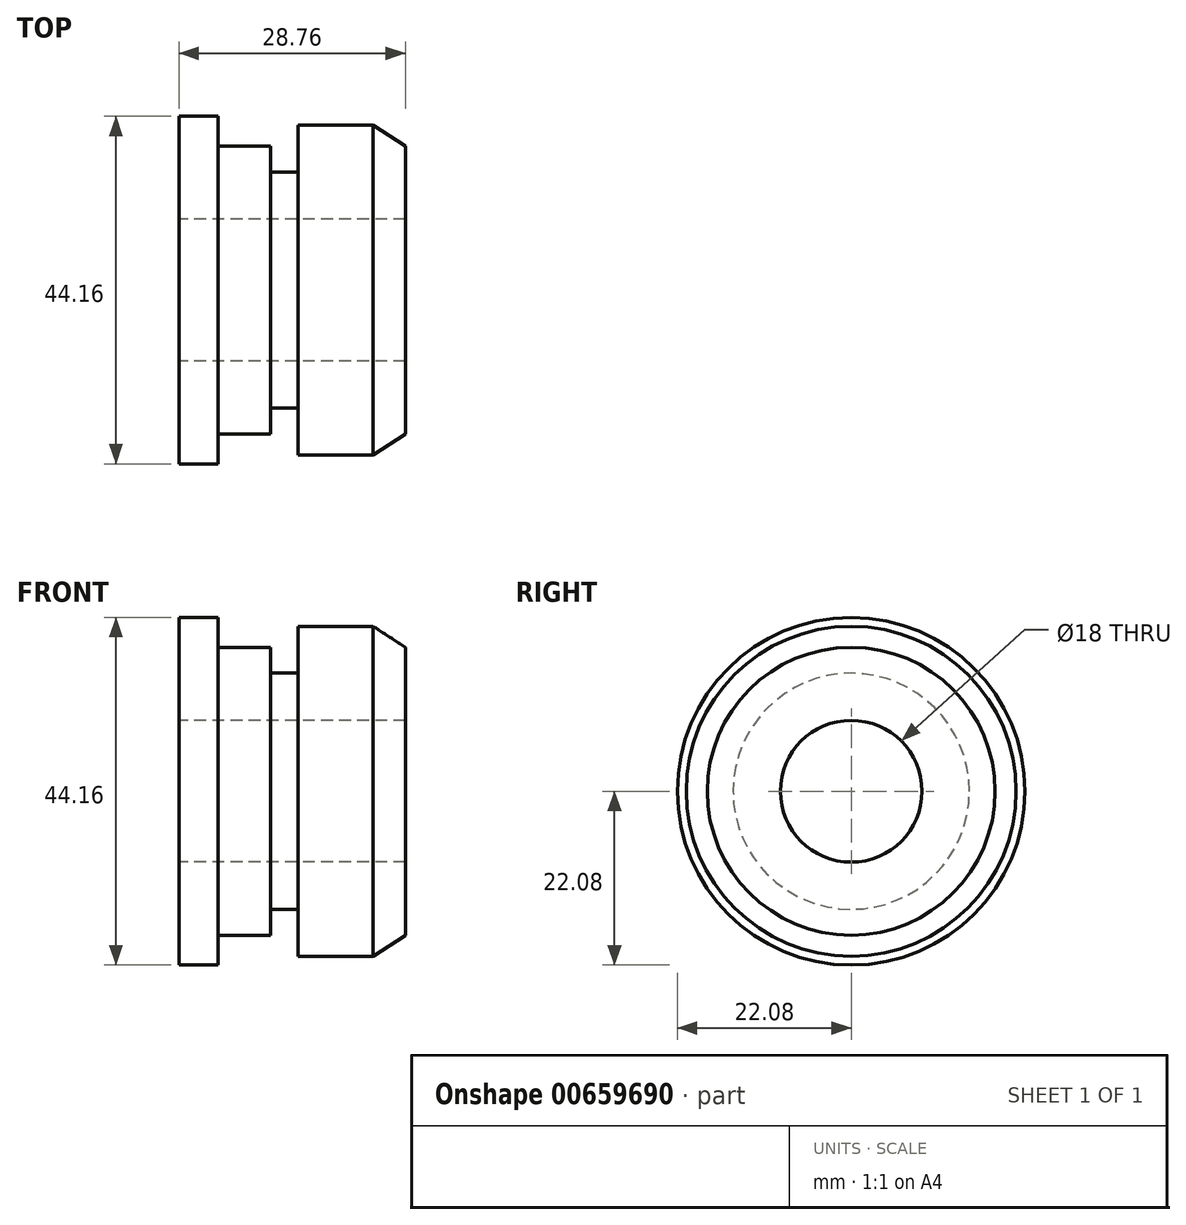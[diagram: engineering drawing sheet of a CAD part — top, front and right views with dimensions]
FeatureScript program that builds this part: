
annotation { "Feature Type Name" : "Feature", "Feature Type Description" : "" }
export const myFeature = defineFeature(function(context is Context, id is Id, definition is map)
    precondition{}
    {
        {
            var Q0;
            Q0=qCreatedBy(makeId("Front.planeOp"),FACE);
            var sketch = newSketch(context, id + "F0", { "sketchPlane" : qUnion([Q0])});
            skLineSegment(sketch, "E0", {"start": v(0, 9) * mm, "end": v(0, 22.08) * mm});
            skLineSegment(sketch, "E1", {"start": v(0, 22.08) * mm, "end": v(5, 22.08) * mm});
            skLineSegment(sketch, "E2", {"start": v(5, 22.08) * mm, "end": v(5, 18.28) * mm});
            skLineSegment(sketch, "E3", {"start": v(5, 18.28) * mm, "end": v(11.62, 18.28) * mm});
            skLineSegment(sketch, "E4", {"start": v(11.62, 18.28) * mm, "end": v(11.62, 15) * mm});
            skLineSegment(sketch, "E5", {"start": v(11.62, 15) * mm, "end": v(15.12, 15) * mm});
            skLineSegment(sketch, "E6", {"start": v(15.12, 15) * mm, "end": v(15.12, 20.95) * mm});
            skLineSegment(sketch, "E7", {"start": v(15.12, 20.95) * mm, "end": v(24.68, 20.95) * mm});
            skLineSegment(sketch, "E8", {"start": v(24.68, 20.95) * mm, "end": v(28.76, 18.28) * mm});
            skLineSegment(sketch, "E9", {"start": v(28.76, 18.28) * mm, "end": v(28.76, 9) * mm});
            skLineSegment(sketch, "E10", {"start": v(28.76, 9) * mm, "end": v(0, 9) * mm});
            skLineSegment(sketch, "E11", {"start": v(-10.48, 0) * mm, "end": v(35.23, 0) * mm});
            skSolve(sketch);
        }
        {
            var Q0;
            Q0=makeQuery(id+"F0.imprint","IMPRINT",FACE,{"disambiguationData":[TD([[makeQuery(id+"F0.imprint","IMPRINT",EDGE,{"derivedFrom":sQuery(id+"F0.wireOp",EDGE,"E0")}),-1.0]])]});
            var Q1;
            Q1=sQuery(id+"F0.wireOp",EDGE,"E11");
            revolve(context, id + "F1", {"entities" : qUnion([Q0]), "axis" : qUnion([Q1]), "revolveType" : RevolveType.FULL});
        }
    });
